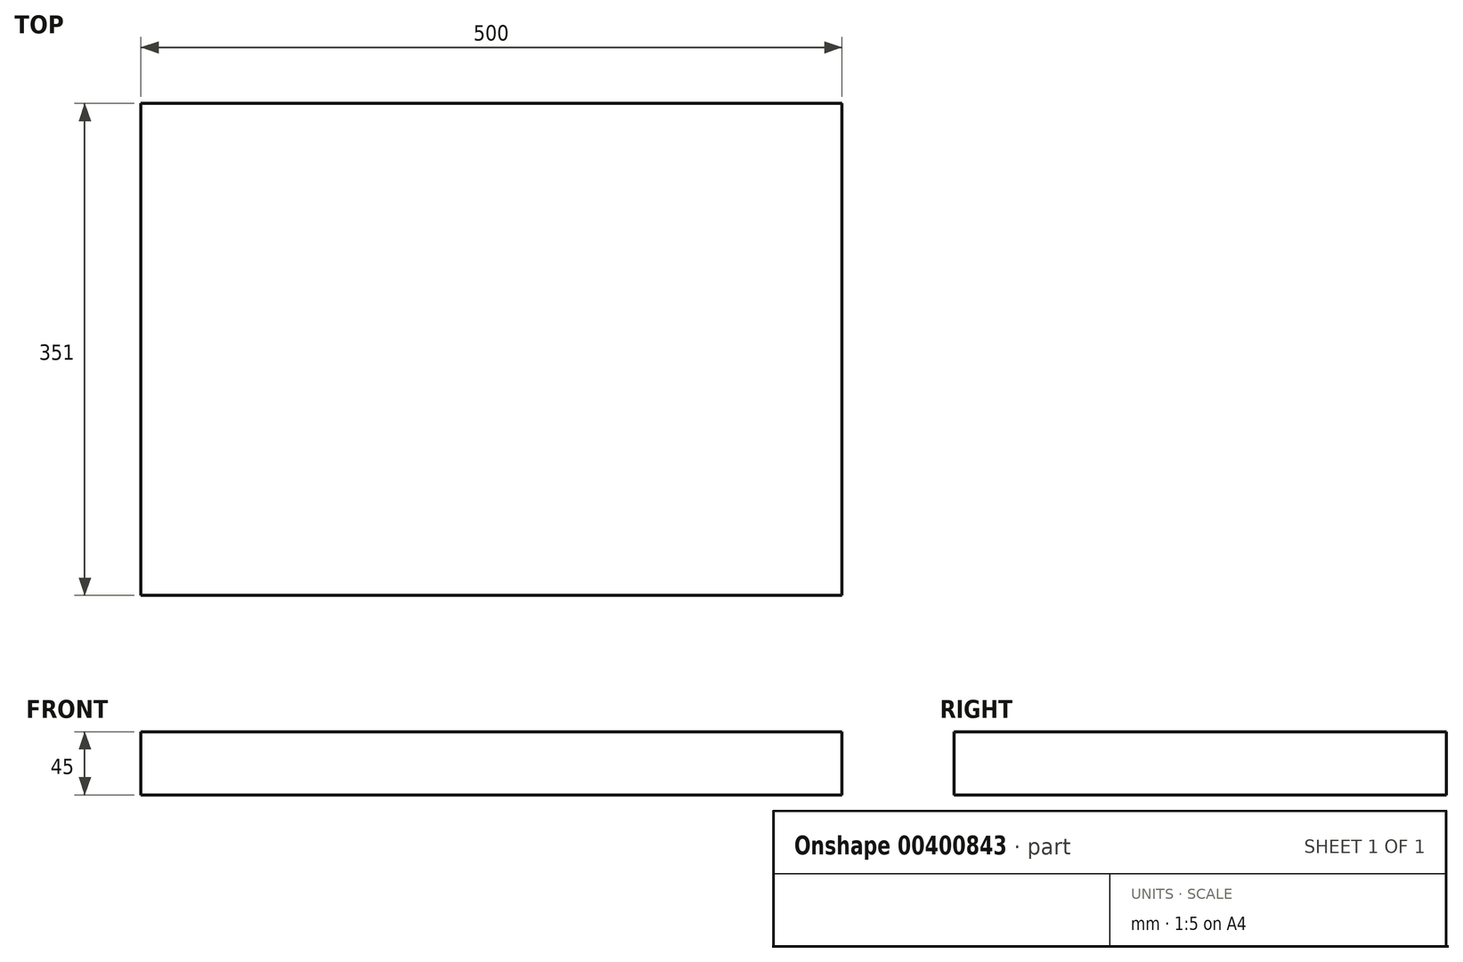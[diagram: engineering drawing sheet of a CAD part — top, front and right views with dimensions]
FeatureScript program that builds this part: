
annotation { "Feature Type Name" : "Feature", "Feature Type Description" : "" }
export const myFeature = defineFeature(function(context is Context, id is Id, definition is map)
    precondition{}
    {
        {
            var Q0;
            Q0=qCreatedBy(makeId("Top.planeOp"),FACE);
            var sketch = newSketch(context, id + "F0", { "sketchPlane" : qUnion([Q0])});
            skLineSegment(sketch, "E0.bottom", {"start": v(250, 175.5) * mm, "end": v(-250, 175.5) * mm});
            skLineSegment(sketch, "E0.top", {"start": v(250, -175.5) * mm, "end": v(-250, -175.5) * mm});
            skLineSegment(sketch, "E0.left", {"start": v(250, 175.5) * mm, "end": v(250, -175.5) * mm});
            skLineSegment(sketch, "E0.right", {"start": v(-250, 175.5) * mm, "end": v(-250, -175.5) * mm});
            skPoint(sketch, "E0.middle", {"position": v(0, 0) * mm});
            skSolve(sketch);
        }
        {
            var Q0;
            Q0=makeQuery(id+"F0.imprint","IMPRINT",FACE,{"disambiguationData":[TD([[makeQuery(id+"F0.imprint","IMPRINT",EDGE,{"derivedFrom":sQuery(id+"F0.wireOp",EDGE,"E0.bottom")}),1.0]])]});
            extrude(context, id + "F1", {"entities" : qUnion([Q0]), "endBound" : BoundingType.SYMMETRIC, "depth" : 45 * mm});
        }
        {
            var Q0;
            Q0=makeQuery(id+"F1.opExtrude","SWEPT_FACE",FACE,{"disambiguationData":[OSD([sQuery(id+"F0.wireOp",EDGE,"E0.top")])]});
            var sketch = newSketch(context, id + "F2", { "sketchPlane" : qUnion([Q0])});
            skLineSegment(sketch, "E1", {"start": v(-250, 22.5) * mm, "end": v(-180, 22.5) * mm});
            skLineSegment(sketch, "E2", {"start": v(-180, 22.5) * mm, "end": v(-215, 22.5) * mm});
            skArc(sketch, "E3", {"start": v(-215, 22.5) * mm, "mid": v(-204.25, -2.74) * mm, "end": v(-178.61, -12.47) * mm});
            skSolve(sketch);
        }
        {
            var Q0;
            Q0=sQuery(id+"F2.wireOp",EDGE,"E3");
            extrude(context, id + "F3", {"bodyType" : ToolBodyType.SURFACE, "surfaceEntities" : qUnion([Q0]), "oppositeDirection" : true, "depth" : 351 * mm});
        }
        {
            var Q0;
            Q0=makeQuery(id+"F3.opExtrude","SWEPT_BODY",BODY,{"disambiguationData":[OSD([sQuery(id+"F2.wireOp",EDGE,"E3")])]});
            var Q1;
            Q1=qCreatedBy(makeId("Right.planeOp"),FACE);
            mirror(context, id + "F4", {"entities" : qUnion([Q0]), "mirrorPlane" : qUnion([Q1])});
        }
        {
            var Q0;
            Q0=makeQuery(id+"F1.opExtrude","SWEPT_FACE",FACE,{"disambiguationData":[OSD([sQuery(id+"F0.wireOp",EDGE,"E0.left")])]});
            var sketch = newSketch(context, id + "F5", { "sketchPlane" : qUnion([Q0])});
            skLineSegment(sketch, "E4", {"start": v(-175.5, 22.5) * mm, "end": v(-105.5, 22.5) * mm});
            skLineSegment(sketch, "E5", {"start": v(-105.5, 22.5) * mm, "end": v(-140.5, 22.5) * mm});
            skArc(sketch, "E6", {"start": v(-140.5, 22.5) * mm, "mid": v(-130.25, -2.25) * mm, "end": v(-105.5, -12.5) * mm});
            skSolve(sketch);
        }
        {
            var Q0;
            Q0=sQuery(id+"F5.wireOp",EDGE,"E6");
            extrude(context, id + "F6", {"bodyType" : ToolBodyType.SURFACE, "surfaceEntities" : qUnion([Q0]), "oppositeDirection" : true, "depth" : 500 * mm});
        }
        {
            var Q0;
            Q0=makeQuery(id+"F6.opExtrude","SWEPT_BODY",BODY,{"disambiguationData":[OSD([sQuery(id+"F5.wireOp",EDGE,"E6")])]});
            var Q1;
            Q1=qCreatedBy(makeId("Front.planeOp"),FACE);
            mirror(context, id + "F7", {"entities" : qUnion([Q0]), "mirrorPlane" : qUnion([Q1])});
        }
    });
